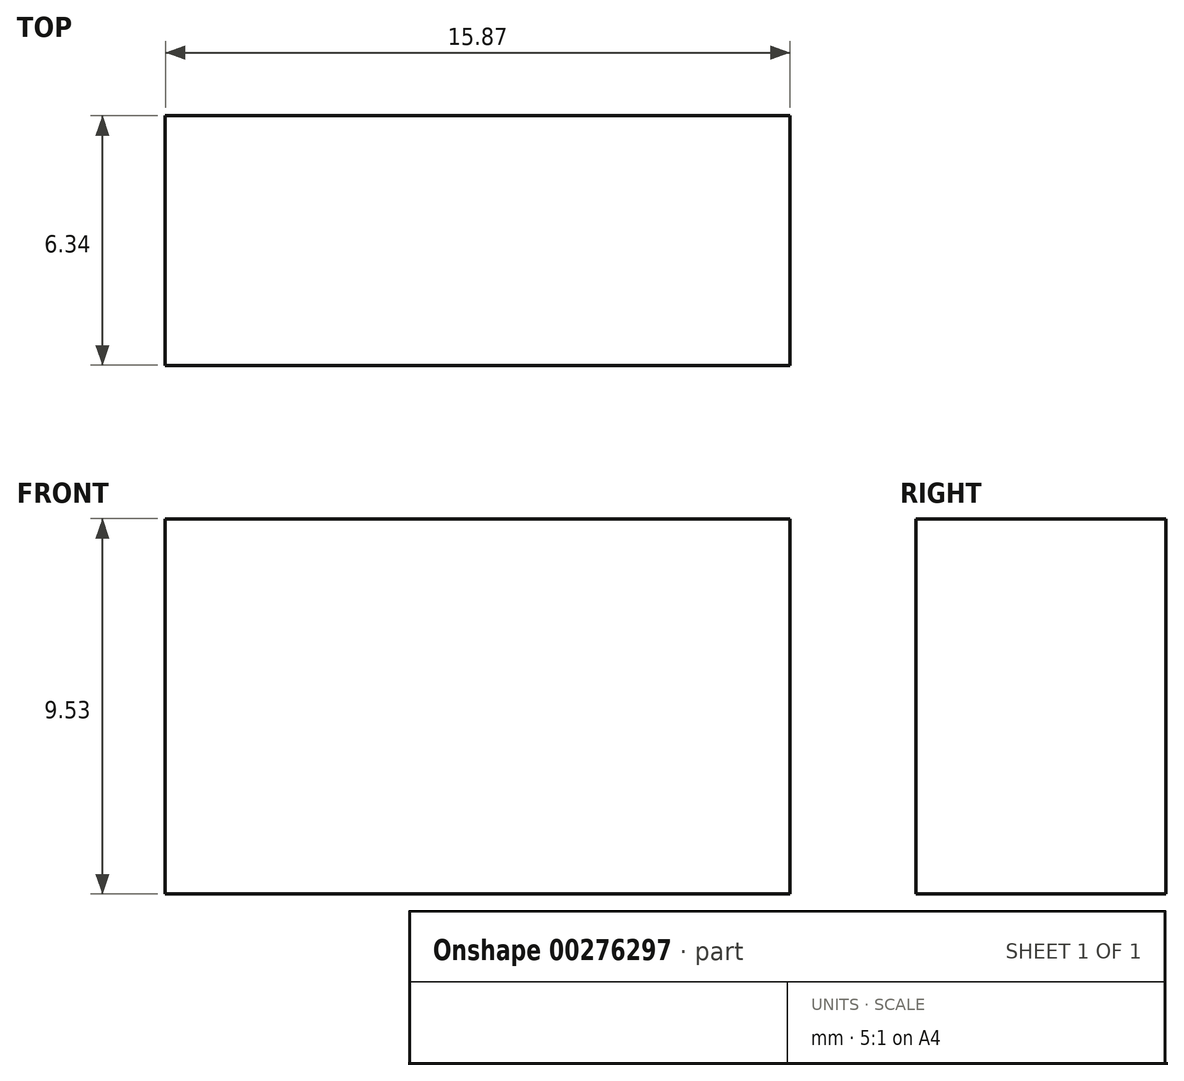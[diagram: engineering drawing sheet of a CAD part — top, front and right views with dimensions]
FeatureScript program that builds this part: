
annotation { "Feature Type Name" : "Feature", "Feature Type Description" : "" }
export const myFeature = defineFeature(function(context is Context, id is Id, definition is map)
    precondition{}
    {
        {
            var Q0;
            Q0=qCreatedBy(makeId("Front.planeOp"),FACE);
            var sketch = newSketch(context, id + "F0", { "sketchPlane" : qUnion([Q0])});
            skLineSegment(sketch, "E0.bottom", {"start": v(-40.45, 15.03) * mm, "end": v(-24.58, 15.03) * mm});
            skLineSegment(sketch, "E0.top", {"start": v(-40.45, 24.56) * mm, "end": v(-24.58, 24.56) * mm});
            skLineSegment(sketch, "E0.left", {"start": v(-40.45, 15.03) * mm, "end": v(-40.45, 24.56) * mm});
            skLineSegment(sketch, "E0.right", {"start": v(-24.58, 15.03) * mm, "end": v(-24.58, 24.56) * mm});
            skPoint(sketch, "E0.middle", {"position": v(-32.52, 19.8) * mm});
            skSolve(sketch);
        }
        {
            var Q0;
            Q0=makeQuery(id+"F0.imprint","IMPRINT",FACE,{"disambiguationData":[TD([[makeQuery(id+"F0.imprint","IMPRINT",EDGE,{"derivedFrom":sQuery(id+"F0.wireOp",EDGE,"E0.bottom")}),1.0]])]});
            extrude(context, id + "F1", {"entities" : qUnion([Q0]), "endBound" : BoundingType.SYMMETRIC, "depth" : 6.35 * mm});
        }
    });
